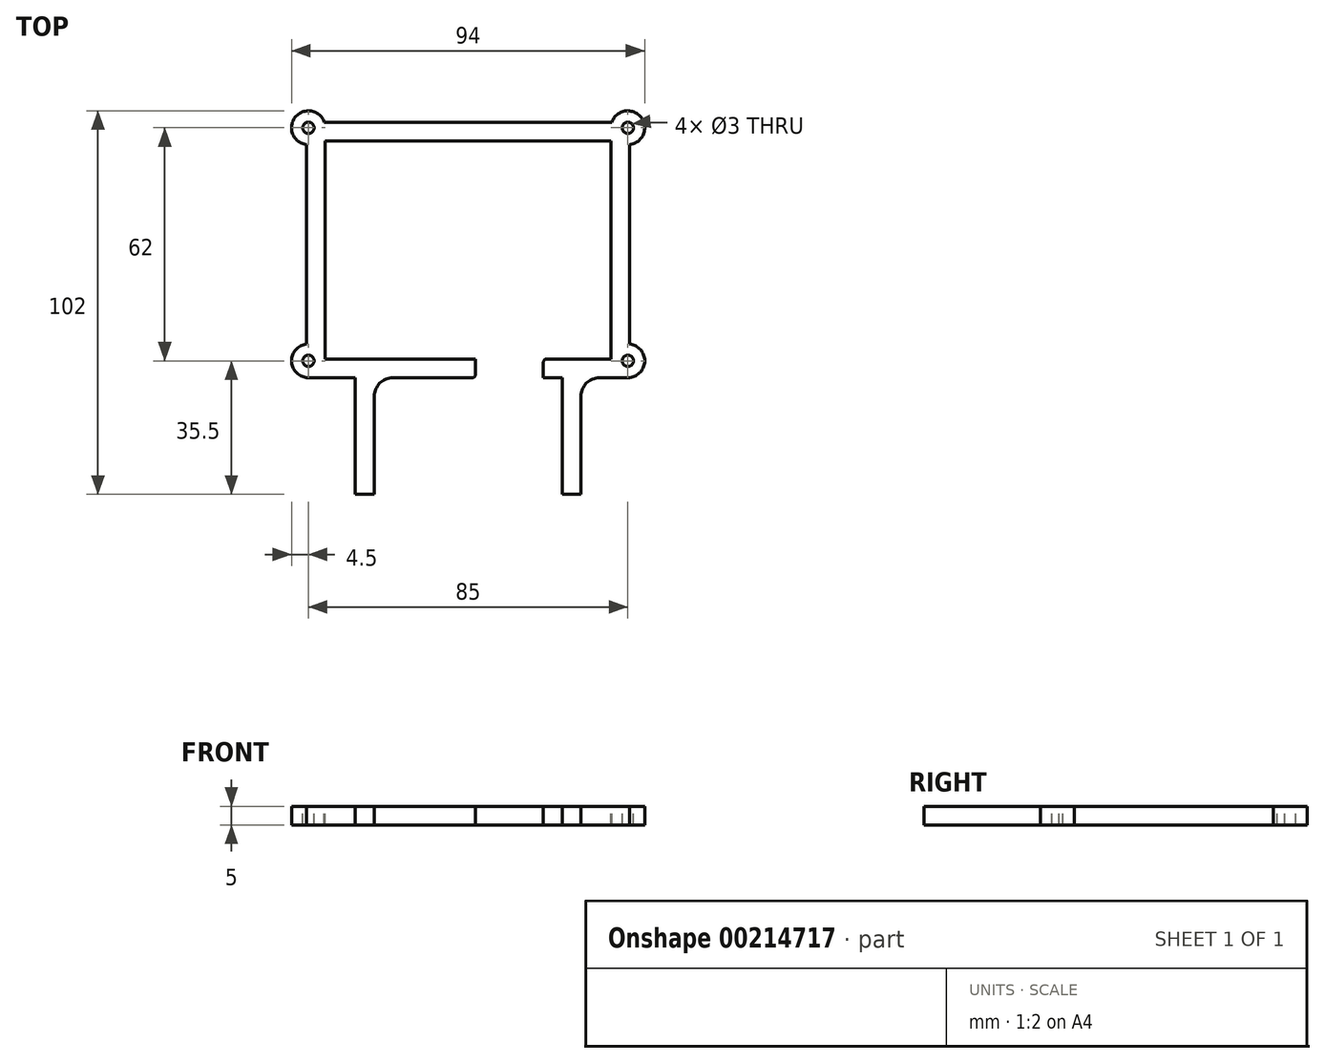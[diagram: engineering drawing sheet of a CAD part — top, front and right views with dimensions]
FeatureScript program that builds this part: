
annotation { "Feature Type Name" : "Feature", "Feature Type Description" : "" }
export const myFeature = defineFeature(function(context is Context, id is Id, definition is map)
    precondition{}
    {
        {
            var Q0;
            Q0=qCreatedBy(makeId("Top.planeOp"),FACE);
            var sketch = newSketch(context, id + "F0", { "sketchPlane" : qUnion([Q0])});
            skLineSegment(sketch, "E0.bottom", {"start": v(43, -34) * mm, "end": v(-43, -34) * mm});
            skLineSegment(sketch, "E0.top", {"start": v(43, 34) * mm, "end": v(-43, 34) * mm});
            skLineSegment(sketch, "E0.left", {"start": v(43, -34) * mm, "end": v(43, 34) * mm});
            skLineSegment(sketch, "E0.right", {"start": v(-43, -34) * mm, "end": v(-43, 34) * mm});
            skPoint(sketch, "E0.middle", {"position": v(0, 0) * mm});
            skSolve(sketch);
        }
        {
            var Q0;
            Q0 = qSketchRegion(id + "F0", true);
            extrude(context, id + "F1", {"entities" : qUnion([Q0]), "depth" : 5 * mm});
        }
        {
            var Q0;
            Q0=makeQuery(id+"F1.opExtrude","CAP_FACE",FACE,{"disambiguationData":[OSD([sQuery(id+"F0.wireOp",EDGE,"E0.bottom"),sQuery(id+"F0.wireOp",EDGE,"E0.top"),sQuery(id+"F0.wireOp",EDGE,"E0.left"),sQuery(id+"F0.wireOp",EDGE,"E0.right")])],"isStart":false});
            var sketch = newSketch(context, id + "F2", { "sketchPlane" : qUnion([Q0])});
            skLineSegment(sketch, "E1.bottom", {"start": v(38, -29) * mm, "end": v(-38, -29) * mm});
            skLineSegment(sketch, "E1.top", {"start": v(38, 29) * mm, "end": v(-38, 29) * mm});
            skLineSegment(sketch, "E1.left", {"start": v(38, -29) * mm, "end": v(38, 29) * mm});
            skLineSegment(sketch, "E1.right", {"start": v(-38, -29) * mm, "end": v(-38, 29) * mm});
            skPoint(sketch, "E1.middle", {"position": v(0, 0) * mm});
            skSolve(sketch);
        }
        {
            var Q0;
            Q0 = qSketchRegion(id + "F2", true);
            extrude(context, id + "F3", {"entities" : qUnion([Q0]), "operationType" : NewBodyOperationType.REMOVE, "endBound" : BoundingType.UP_TO_NEXT, "oppositeDirection" : true, "depth" : 25 * mm});
        }
        {
            var Q0;
            Q0=makeQuery(id+"F1.opExtrude","CAP_FACE",FACE,{"disambiguationData":[OSD([sQuery(id+"F0.wireOp",EDGE,"E0.bottom"),sQuery(id+"F0.wireOp",EDGE,"E0.top"),sQuery(id+"F0.wireOp",EDGE,"E0.left"),sQuery(id+"F0.wireOp",EDGE,"E0.right")])],"isStart":false});
            var sketch = newSketch(context, id + "F4", { "sketchPlane" : qUnion([Q0])});
            skLineSegment(sketch, "E2.bottom", {"start": v(2, -29) * mm, "end": v(20, -29) * mm});
            skLineSegment(sketch, "E2.top", {"start": v(2, -34) * mm, "end": v(20, -34) * mm});
            skLineSegment(sketch, "E2.left", {"start": v(2, -29) * mm, "end": v(2, -34) * mm});
            skLineSegment(sketch, "E2.right", {"start": v(20, -29) * mm, "end": v(20, -34) * mm});
            skSolve(sketch);
        }
        {
            var Q0;
            Q0 = qSketchRegion(id + "F4", true);
            extrude(context, id + "F5", {"entities" : qUnion([Q0]), "operationType" : NewBodyOperationType.REMOVE, "endBound" : BoundingType.UP_TO_NEXT, "oppositeDirection" : true, "depth" : 25 * mm});
        }
        {
            var Q0;
            Q0=makeQuery(id+"F1.opExtrude","CAP_FACE",FACE,{"disambiguationData":[OSD([sQuery(id+"F0.wireOp",EDGE,"E0.bottom"),sQuery(id+"F0.wireOp",EDGE,"E0.top"),sQuery(id+"F0.wireOp",EDGE,"E0.left"),sQuery(id+"F0.wireOp",EDGE,"E0.right")])],"isStart":false});
            var sketch = newSketch(context, id + "F6", { "sketchPlane" : qUnion([Q0])});
            skLineSegment(sketch, "E3.bottom", {"start": v(42.5, -32.5) * mm, "end": v(-42.5, -32.5) * mm, "construction": true});
            skLineSegment(sketch, "E3.top", {"start": v(42.5, 32.5) * mm, "end": v(-42.5, 32.5) * mm, "construction": true});
            skLineSegment(sketch, "E3.left", {"start": v(42.5, -32.5) * mm, "end": v(42.5, 32.5) * mm, "construction": true});
            skLineSegment(sketch, "E3.right", {"start": v(-42.5, -32.5) * mm, "end": v(-42.5, 32.5) * mm, "construction": true});
            skPoint(sketch, "E3.middle", {"position": v(0, 0) * mm});
            skCircle(sketch, "E4", {"center": v(-42.5, 32.5) * mm, "radius": 4.5 * mm});
            skCircle(sketch, "E5", {"center": v(42.5, 32.5) * mm, "radius": 4.5 * mm});
            skCircle(sketch, "E6", {"center": v(-42.5, -29.5) * mm, "radius": 4.5 * mm});
            skCircle(sketch, "E7", {"center": v(42.5, -29.5) * mm, "radius": 4.5 * mm});
            skLineSegment(sketch, "E8", {"start": v(-42.5, -29.5) * mm, "end": v(42.5, -29.5) * mm, "construction": true});
            skSolve(sketch);
        }
        {
            var Q0;
            Q0 = qSketchRegion(id + "F6", true);
            extrude(context, id + "F7", {"entities" : qUnion([Q0]), "operationType" : NewBodyOperationType.ADD, "oppositeDirection" : true, "depth" : 5 * mm});
        }
        {
            var Q0;
            Q0=makeQuery(id+"F7.boolean.opBoolean","MERGE",FACE,{"derivedFrom":[makeQuery(id+"F1.opExtrude","CAP_FACE",FACE,{"disambiguationData":[OSD([sQuery(id+"F0.wireOp",EDGE,"E0.bottom"),sQuery(id+"F0.wireOp",EDGE,"E0.top"),sQuery(id+"F0.wireOp",EDGE,"E0.left"),sQuery(id+"F0.wireOp",EDGE,"E0.right")])],"isStart":false}),makeQuery(id+"F7.opExtrude","CAP_FACE",FACE,{"disambiguationData":[OSD([sQuery(id+"F6.wireOp",EDGE,"E4")])],"isStart":true}),makeQuery(id+"F7.opExtrude","CAP_FACE",FACE,{"disambiguationData":[OSD([sQuery(id+"F6.wireOp",EDGE,"E5")])],"isStart":true}),makeQuery(id+"F7.opExtrude","CAP_FACE",FACE,{"disambiguationData":[OSD([sQuery(id+"F6.wireOp",EDGE,"sF2ayLWO-sgky-sRq5-ePZq-n1bWY39a1GB6")])],"isStart":true}),makeQuery(id+"F7.opExtrude","CAP_FACE",FACE,{"disambiguationData":[OSD([sQuery(id+"F6.wireOp",EDGE,"2T9JyqHt-AarN-y7sK-YD04-87LepLVi80L8")])],"isStart":true})]});
            var sketch = newSketch(context, id + "F8", { "sketchPlane" : qUnion([Q0])});
            skCircle(sketch, "E9", {"center": v(-42.5, 32.5) * mm, "radius": 1.5 * mm});
            skCircle(sketch, "E10", {"center": v(-42.5, -29.5) * mm, "radius": 1.5 * mm});
            skCircle(sketch, "E11", {"center": v(42.5, -29.5) * mm, "radius": 1.5 * mm});
            skCircle(sketch, "E12", {"center": v(42.5, 32.5) * mm, "radius": 1.5 * mm});
            skSolve(sketch);
        }
        {
            var Q0;
            Q0 = qSketchRegion(id + "F8", true);
            extrude(context, id + "F9", {"entities" : qUnion([Q0]), "operationType" : NewBodyOperationType.REMOVE, "endBound" : BoundingType.UP_TO_NEXT, "oppositeDirection" : true, "depth" : 25 * mm});
        }
        {
            var Q0;
            Q0=makeQuery(id+"F5.boolean.opBoolean","COPY",EDGE,{"derivedFrom":makeQuery(id+"F5.opExtrude","SWEPT_EDGE",EDGE,{"disambiguationData":[OSD([sQuery(id+"F2.wireOp",EDGE,"E1.bottom"),sQuery(id+"F4.wireOp",EDGE,"E2.bottom"),sQuery(id+"F4.wireOp",EDGE,"E2.right")])]})});
            var Q1;
            Q1=makeQuery(id+"F5.boolean.opBoolean","COPY",EDGE,{"derivedFrom":makeQuery(id+"F5.opExtrude","SWEPT_EDGE",EDGE,{"disambiguationData":[OSD([sQuery(id+"F0.wireOp",EDGE,"E0.bottom"),sQuery(id+"F4.wireOp",EDGE,"E2.top"),sQuery(id+"F4.wireOp",EDGE,"E2.right")])]})});
            var Q2;
            Q2=makeQuery(id+"F5.boolean.opBoolean","COPY",EDGE,{"derivedFrom":makeQuery(id+"F5.opExtrude","SWEPT_EDGE",EDGE,{"disambiguationData":[OSD([sQuery(id+"F2.wireOp",EDGE,"E1.bottom"),sQuery(id+"F4.wireOp",EDGE,"E2.bottom"),sQuery(id+"F4.wireOp",EDGE,"E2.left")])]})});
            var Q3;
            Q3=makeQuery(id+"F5.boolean.opBoolean","COPY",EDGE,{"derivedFrom":makeQuery(id+"F5.opExtrude","SWEPT_EDGE",EDGE,{"disambiguationData":[OSD([sQuery(id+"F0.wireOp",EDGE,"E0.bottom"),sQuery(id+"F4.wireOp",EDGE,"E2.top"),sQuery(id+"F4.wireOp",EDGE,"E2.left")])]})});
            fillet(context, id + "F10", {"entities" : qUnion([Q0, Q1, Q2, Q3]), "radius" : 1 * mm, "tangentPropagation" : true, "allowEdgeOverflow" : false});
        }
        {
            var Q0;
            {var subQ0=sQuery(id+"F0.wireOp",EDGE,"E0.right");var subQ3=sQuery(id+"F0.wireOp",EDGE,"E0.bottom");Q0=makeQuery(id+"F5.boolean.opBoolean","SPLIT",FACE,{"disambiguationData":[TD([makeQuery(id+"F1.opExtrude","SWEPT_FACE",FACE,{"disambiguationData":[OSD([subQ0])]})])],"derivedFrom":makeQuery(id+"F1.opExtrude","SWEPT_FACE",FACE,{"disambiguationData":[OSD([subQ3])]})});}
            var sketch = newSketch(context, id + "F11", { "sketchPlane" : qUnion([Q0])});
            skLineSegment(sketch, "E13.bottom", {"start": v(-30, 5) * mm, "end": v(-25, 5) * mm});
            skLineSegment(sketch, "E13.top", {"start": v(-30, 0) * mm, "end": v(-25, 0) * mm});
            skLineSegment(sketch, "E13.left", {"start": v(-30, 5) * mm, "end": v(-30, 0) * mm});
            skLineSegment(sketch, "E13.right", {"start": v(-25, 5) * mm, "end": v(-25, 0) * mm});
            skLineSegment(sketch, "E14.bottom", {"start": v(25, 5) * mm, "end": v(30, 5) * mm});
            skLineSegment(sketch, "E14.top", {"start": v(25, 0) * mm, "end": v(30, 0) * mm});
            skLineSegment(sketch, "E14.left", {"start": v(25, 5) * mm, "end": v(25, 0) * mm});
            skLineSegment(sketch, "E14.right", {"start": v(30, 5) * mm, "end": v(30, 0) * mm});
            skSolve(sketch);
        }
        {
            var Q0;
            Q0 = qSketchRegion(id + "F11", true);
            extrude(context, id + "F12", {"entities" : qUnion([Q0]), "operationType" : NewBodyOperationType.ADD, "depth" : (25 + 6) * mm});
        }
        {
            var Q0;
            Q0=makeQuery(id+"F12.opExtrude","CAP_EDGE",EDGE,{"disambiguationData":[OSD([sQuery(id+"F11.wireOp",EDGE,"E14.left")])],"isStart":true});
            var Q1;
            Q1=makeQuery(id+"F12.opExtrude","CAP_EDGE",EDGE,{"disambiguationData":[OSD([sQuery(id+"F11.wireOp",EDGE,"E13.right")])],"isStart":true});
            var Q2;
            Q2=makeQuery(id+"F12.opExtrude","CAP_EDGE",EDGE,{"disambiguationData":[OSD([sQuery(id+"F11.wireOp",EDGE,"E14.right")])],"isStart":true});
            var Q3;
            Q3=makeQuery(id+"F12.opExtrude","CAP_EDGE",EDGE,{"disambiguationData":[OSD([sQuery(id+"F11.wireOp",EDGE,"E13.left")])],"isStart":true});
            fillet(context, id + "F13", {"entities" : qUnion([Q0, Q1, Q2, Q3]), "radius" : 5 * mm, "tangentPropagation" : true, "allowEdgeOverflow" : false});
        }
    });
